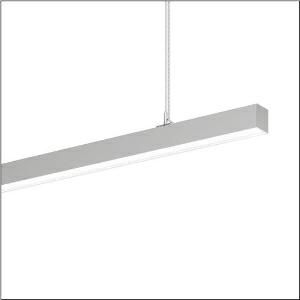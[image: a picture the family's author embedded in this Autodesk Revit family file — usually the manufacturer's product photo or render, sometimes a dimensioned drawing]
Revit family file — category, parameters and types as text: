
# Revit family: silica_r__21_51mx33tctds_657e
name_source: partatom
category: Lighting Fixtures
units: mm (PartAtom-declared; Revit-internal decimal feet)

## family parameters
Cut with Voids When Loaded = No
Host = Face
Light Source = No
Part Type = Normal
Room Calculation Point = No
Round Connector Dimension = Use Diameter
Shared = No

## types (1)
- --- (1 x LED, 14340 lm, 134.7 W, 6500K)
    Apparent Load = 135 VA
    CIE Flux Codes = 78 96 99 56 100
    Color Rendering = 80
    Color Temperature = 6500K
    Default Elevation = 1800 mm
    Description = Silica® 21, office luminaire, primary optical cover: prismatic diffuser, of PMMA, CAT 2 (L<= 3000cd/m²), light emission: direct/indirect distribution, primary light characteristic: symmetric, installation type: suspended mounting, LED, rated luminous flux: 14.340lm, luminous efficacy: 101lm/W, light colour: 8tw, colour temperature: 2700..6500K, control gear: ECG DALI, with terminal, 3+2-pole, max. 2.5mm², mains connection: 220..240V, AC, 50/60Hz, rated input power: 141.4W, luminaire housing, of aluminium, metallic grey (RAL 9006), length: 3.004mm, width: 53mm, height: 53mm, protection rating (complete): IP20, insulation class (complete): insulation class I (protective earthing), certification: CE, permissible operating ambient temperature: 0..+35°C, standard: EN 50419, packaging unit: 1 piece
    Height = 53 mm
    Lamp = 1 x LED
    Lamp Light Flux = 14340 lm
    Lamp Power = 134.7 W
    Lamp count = 1
    Length = 3004 mm
    Luminous efficacy = 106 lm/W
    Manufacturer = Siteco
    ModVariant = No
    Model = 51MX33TCTDS
    Mounting Place = Ceiling
    Mounting Type = Pendant
    Number of Poles = 1
    OnlyDefault = Yes
    Power Factor = 1
    Product Name = Silica® 21
    Product group = office luminaire | ceiling pendant
    ProductGroupID = 902
    Protection Class = Protection class I
    Protection Degree = IP 20
    RLX_Detail_Level = 1
    RLX_Emergency_Light_Flux = 0 lm
    RLX_Emergency_Type = 0
    RLX_Emergency_Type_DB = No
    RlxData = <blob elided: 20105 chars, md5=c2681cd1>
    Socket = socket
    Standby Power = 0 W
    System Light Flux = 14340 lm
    System Power = 135 W
    Type Comments = individual setting
    Type Image = l_1313621.jpg
    URL = http://relux.com
    VarID = @adj_089103
    Voltage = 0 V
    Weight = 0.00 kg
    Width = 53 mm

## geometry (parser evidence)
native form markers: Blend x4, Sweep x12
no freeform markers — native parametric forms only
